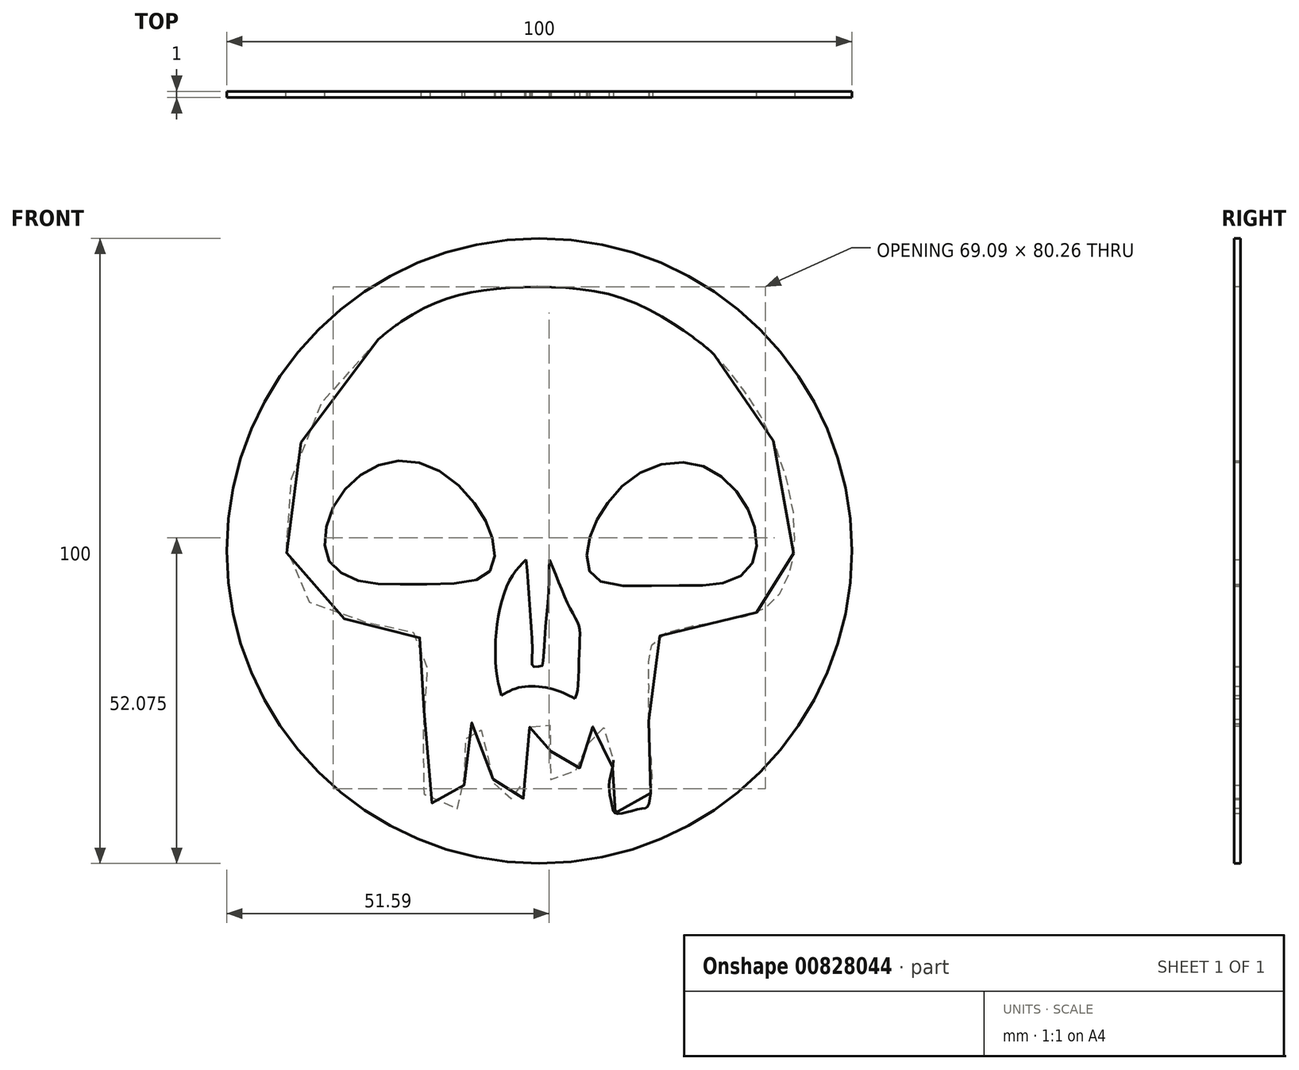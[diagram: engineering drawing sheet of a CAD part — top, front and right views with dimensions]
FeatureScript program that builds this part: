
annotation { "Feature Type Name" : "Feature", "Feature Type Description" : "" }
export const myFeature = defineFeature(function(context is Context, id is Id, definition is map)
    precondition{}
    {
        {
            var Q0;
            Q0=qCreatedBy(makeId("Front.planeOp"),FACE);
            var sketch = newSketch(context, id + "F0", { "sketchPlane" : qUnion([Q0])});
            skSolve(sketch);
        }
        {
            var Q0;
            Q0=qCreatedBy(makeId("Front.planeOp"),FACE);
            var sketch = newSketch(context, id + "F1", { "sketchPlane" : qUnion([Q0])});
            skFitSpline(sketch, "E0", {"points": [v(0, 42.21) * mm, v(-11.72, 41.16) * mm, v(-21.43, 37.1) * mm, v(-30.9, 28.7) * mm, v(-37.63, 18.55) * mm, v(-40.34, 7.41) * mm, v(-40.46, 0) * mm, v(-38.7, -6.08) * mm, v(-33.24, -10.3) * mm, v(-27.66, -11.36) * mm, v(-22.63, -12.3) * mm, v(-19.43, -13.56) * mm, v(-17.47, -17.28) * mm, v(-17.89, -18.61) * mm, v(-18.37, -24.15) * mm, v(-18.87, -33.53) * mm, v(-18.37, -39.08) * mm, v(-15.65, -41.04) * mm, v(-13.56, -41.23) * mm, v(-12.56, -41.1) * mm, v(-12.24, -39.83) * mm, v(-11.98, -36.56) * mm, v(-12.24, -33.56) * mm, v(-12.4, -32.36) * mm, v(-11.05, -28.18) * mm, v(-10.45, -26.99) * mm, v(-9.7, -27.44) * mm, v(-8.96, -31.02) * mm, v(-7.32, -36.7) * mm, v(-6.87, -39.23) * mm, v(-6.65, -39.73) * mm, v(-5.23, -39.68) * mm, v(-3.29, -39.68) * mm, v(-2.53, -39.55) * mm, v(-2.4, -38.04) * mm, v(-2.24, -35.2) * mm, v(-1.5, -28.63) * mm, v(-1.5, -27.73) * mm, v(-0.52, -27.73) * mm, v(0.82, -27.77) * mm, v(1.64, -27.85) * mm, v(1.83, -28.82) * mm, v(1.83, -36.32) * mm, v(1.83, -37.22) * mm, v(2.2, -37.51) * mm, v(4.52, -35.98) * mm, v(7.76, -33.74) * mm, v(8.03, -33.07) * mm, v(7.95, -31.4) * mm, v(7.76, -28.4) * mm, v(8.06, -28.18) * mm, v(10, -28.1) * mm, v(10.49, -28.48) * mm, v(10.71, -29.34) * mm, v(11.72, -32.18) * mm, v(11.65, -35.01) * mm, v(11.19, -37.22) * mm, v(11.34, -39.35) * mm, v(11.66, -40.83) * mm, v(11.88, -41.68) * mm, v(12.54, -42.05) * mm, v(14.48, -41.68) * mm, v(16.62, -41.17) * mm, v(17.3, -40.96) * mm, v(17.7, -39.33) * mm, v(18.08, -36.87) * mm, v(17.9, -33.23) * mm, v(17.56, -29.62) * mm, v(17.53, -20.49) * mm, v(17.69, -15.86) * mm, v(19.63, -13.4) * mm, v(27.92, -11.46) * mm, v(34.41, -9.97) * mm, v(38, -7.5) * mm, v(40, -3.47) * mm, v(40.68, -0.56) * mm, v(40.68, 5.93) * mm, v(37.22, 18.07) * mm, v(31.73, 27.06) * mm, v(28.14, 31.23) * mm, v(24.25, 34.4) * mm, v(13.7, 40.27) * mm, v(0, 42.21) * mm]});
            skFitSpline(sketch, "E1", {"points": [v(-25.81, 33.77) * mm, v(-23.7, 24.61) * mm], "startDerivative": vector(2.09, -9.14) * mm, "endDerivative": vector(2.09, -9.14) * mm});
            skFitSpline(sketch, "E2", {"points": [v(-23.7, 24.61) * mm, v(-16.96, 22.97) * mm, v(-11.45, 20.89) * mm], "startDerivative": vector(13.34, -2.84) * mm, "endDerivative": vector(11.13, -4.64) * mm});
            skFitSpline(sketch, "E3", {"points": [v(-11.45, 20.89) * mm, v(-16.96, 25.15) * mm, v(-20.29, 28.25) * mm, v(-21.93, 32.47) * mm, v(-22.05, 36.69) * mm], "startDerivative": vector(-19.63, 15.23) * mm, "endDerivative": vector(0.8, 18.17) * mm});
            skFitSpline(sketch, "E4", {"points": [v(24.54, 34.2) * mm, v(20.63, 30.76) * mm, v(13.63, 26.4) * mm], "startDerivative": vector(-7.1, -7.92) * mm, "endDerivative": vector(-14.38, -8.75) * mm});
            skFitSpline(sketch, "E5", {"points": [v(13.63, 26.4) * mm, v(17.28, 26.57) * mm, v(24.65, 29.42) * mm, v(27.97, 31.4) * mm], "startDerivative": vector(13.04, -1.16) * mm, "endDerivative": vector(9.37, 6.14) * mm});
            skFitSpline(sketch, "E6", {"points": [v(-22.52, 14.42) * mm, v(-15.86, 12.73) * mm, v(-9.82, 6.87) * mm, v(-7.42, 1.72) * mm, v(-7.6, -2.72) * mm, v(-10.97, -4.85) * mm, v(-21.37, -5.34) * mm, v(-28.55, -4.85) * mm, v(-33, -2.45) * mm, v(-34.32, 1.28) * mm, v(-32.9, 7.14) * mm, v(-28.46, 12.2) * mm, v(-22.52, 14.42) * mm]});
            skFitSpline(sketch, "E7.MirrorC", {"points": [v(23.03, 14.16) * mm, v(15.87, 12.34) * mm, v(10.54, 7.13) * mm, v(8.09, 2.17) * mm, v(7.77, -2.53) * mm, v(10.22, -5.05) * mm, v(21.02, -5.55) * mm, v(28.93, -5.23) * mm, v(33.45, -2.91) * mm, v(34.77, 1.48) * mm, v(33.26, 6.88) * mm, v(28.93, 12.03) * mm, v(23.03, 14.16) * mm]});
            skFitSpline(sketch, "E8", {"points": [v(-2.1, -1.4) * mm, v(-4.89, -4.97) * mm, v(-6.96, -13.76) * mm, v(-6.7, -20.35) * mm, v(-6.08, -23.11) * mm], "startDerivative": vector(-12.66, -12.53) * mm, "endDerivative": vector(3.72, -13.83) * mm});
            skFitSpline(sketch, "E9", {"points": [v(-6.08, -23.11) * mm, v(-3.58, -21.94) * mm, v(-0.59, -21.68) * mm, v(2.8, -22.3) * mm, v(5.69, -23.63) * mm], "startDerivative": vector(10.12, 5.73) * mm, "endDerivative": vector(9.93, -5.43) * mm});
            skFitSpline(sketch, "E10", {"points": [v(5.69, -23.63) * mm, v(6.2, -21.26) * mm, v(6.43, -15.07) * mm, v(6.43, -12.27) * mm, v(5.69, -10.63) * mm, v(4.08, -7.34) * mm, v(1.63, -1.42) * mm], "startDerivative": vector(7.54, 13.44) * mm, "endDerivative": vector(-11.31, 26.08) * mm});
            skFitSpline(sketch, "E11", {"points": [v(1.63, -1.42) * mm, v(1.5, -6.3) * mm, v(0.97, -12.47) * mm, v(0.62, -17.8) * mm, v(0.4, -18.42) * mm, v(-0.53, -18.51) * mm, v(-1.11, -18.42) * mm, v(-1.16, -17.31) * mm, v(-1.25, -12.56) * mm, v(-1.69, -6.97) * mm, v(-2.1, -1.4) * mm], "startDerivative": vector(-3.41, -34.26) * mm, "endDerivative": vector(-4.32, 40.08) * mm});
            skCircle(sketch, "E12", {"center": v(0, 0) * mm, "radius": 50 * mm});
            skSolve(sketch);
        }
        {
            var Q0;
            Q0=makeQuery(id+"F1.imprint","IMPRINT",FACE,{"disambiguationData":[TD([[makeQuery(id+"F1.imprint","IMPRINT",EDGE,{"derivedFrom":sQuery(id+"F1.wireOp",EDGE,"E0")}),-1.0]])]});
            var Q1;
            Q1=makeQuery(id+"F1.imprint","IMPRINT",FACE,{"disambiguationData":[TD([[makeQuery(id+"F1.imprint","IMPRINT",EDGE,{"derivedFrom":sQuery(id+"F1.wireOp",EDGE,"E8")}),1.0]])]});
            var Q2;
            Q2=makeQuery(id+"F1.imprint","IMPRINT",FACE,{"disambiguationData":[TD([[makeQuery(id+"F1.imprint","IMPRINT",EDGE,{"derivedFrom":sQuery(id+"F1.wireOp",EDGE,"E6")}),-1.0]])]});
            var Q3;
            Q3=makeQuery(id+"F1.imprint","IMPRINT",FACE,{"disambiguationData":[TD([[makeQuery(id+"F1.imprint","IMPRINT",EDGE,{"derivedFrom":sQuery(id+"F1.wireOp",EDGE,"E7.MirrorC")}),1.0]])]});
            extrude(context, id + "F2", {"entities" : qUnion([Q0, Q1, Q2, Q3]), "depth" : 1 * mm, "offsetDistance" : 25 * mm});
        }
        {
            var Q0;
            Q0=makeQuery(id+"F2.opExtrude","SWEPT_BODY",BODY,{"disambiguationData":[OSD([sQuery(id+"F1.wireOp",EDGE,"E0"),sQuery(id+"F1.wireOp",EDGE,"E1"),sQuery(id+"F1.wireOp",EDGE,"E2"),sQuery(id+"F1.wireOp",EDGE,"E3"),sQuery(id+"F1.wireOp",EDGE,"E4"),sQuery(id+"F1.wireOp",EDGE,"E5"),sQuery(id+"F1.wireOp",EDGE,"E0"),sQuery(id+"F1.wireOp",EDGE,"E12")])]});
            var Q1;
            Q1=makeQuery(id+"F2.opExtrude","SWEPT_BODY",BODY,{"disambiguationData":[OSD([sQuery(id+"F1.wireOp",EDGE,"E6")])]});
            var Q2;
            Q2=makeQuery(id+"F2.opExtrude","SWEPT_BODY",BODY,{"disambiguationData":[OSD([sQuery(id+"F1.wireOp",EDGE,"E7.MirrorC")])]});
            var Q3;
            Q3=makeQuery(id+"F2.opExtrude","SWEPT_BODY",BODY,{"disambiguationData":[OSD([sQuery(id+"F1.wireOp",EDGE,"E8"),sQuery(id+"F1.wireOp",EDGE,"E9"),sQuery(id+"F1.wireOp",EDGE,"E10"),sQuery(id+"F1.wireOp",EDGE,"E11")])]});
            var Q4;
            Q4=qCreatedBy(makeId("Origin.pointOp"),VERTEX);
            transform(context, id + "F3", {"entities" : qUnion([Q0, Q1, Q2, Q3]), "transformType" : TransformType.SCALE_UNIFORMLY, "scale" : 1, "scalePoint" : qUnion([Q4]), "makeCopy" : false});
        }
    });
